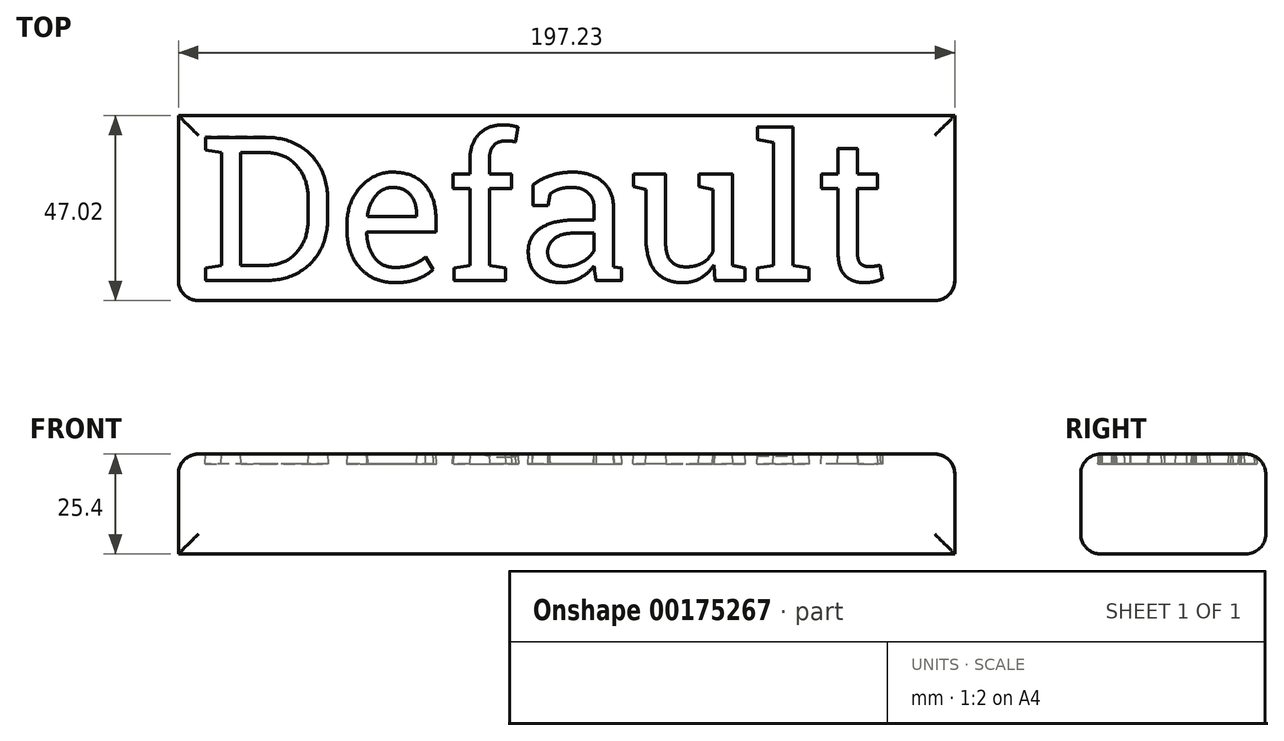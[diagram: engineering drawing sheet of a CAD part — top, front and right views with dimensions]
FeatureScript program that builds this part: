
annotation { "Feature Type Name" : "Feature", "Feature Type Description" : "" }
export const myFeature = defineFeature(function(context is Context, id is Id, definition is map)
    precondition{}
    {
        {
            var Q0;
            Q0=qCreatedBy(makeId("Top.planeOp"),FACE);
            var sketch = newSketch(context, id + "F0", { "sketchPlane" : qUnion([Q0])});
            skLineSegment(sketch, "E0.bottom", {"start": v(-91.51, 20.47) * mm, "end": v(105.72, 20.47) * mm});
            skLineSegment(sketch, "E0.top", {"start": v(-91.51, -26.55) * mm, "end": v(105.72, -26.55) * mm});
            skLineSegment(sketch, "E0.left", {"start": v(-91.51, 20.47) * mm, "end": v(-91.51, -26.55) * mm});
            skLineSegment(sketch, "E0.right", {"start": v(105.72, 20.47) * mm, "end": v(105.72, -26.55) * mm});
            skSolve(sketch);
        }
        {
            var Q0;
            Q0 = qSketchRegion(id + "F0", true);
            extrude(context, id + "F1", {"entities" : qUnion([Q0]), "depth" : 25.4 * mm});
        }
        {
            var Q0;
            Q0=makeQuery(id+"F1.opExtrude","CAP_FACE",FACE,{"disambiguationData":[OSD([sQuery(id+"F0.wireOp",EDGE,"E0.bottom"),sQuery(id+"F0.wireOp",EDGE,"E0.top"),sQuery(id+"F0.wireOp",EDGE,"E0.left"),sQuery(id+"F0.wireOp",EDGE,"E0.right")])],"isStart":false});
            var Q1;
            Q1=makeQuery(id+"F1.opExtrude","SWEPT_FACE",FACE,{"disambiguationData":[OSD([sQuery(id+"F0.wireOp",EDGE,"E0.top")])]});
            var Q2;
            Q2=makeQuery(id+"F1.opExtrude","CAP_EDGE",EDGE,{"disambiguationData":[OSD([sQuery(id+"F0.wireOp",EDGE,"E0.bottom")])],"isStart":true});
            fillet(context, id + "F2", {"entities" : qUnion([Q0, Q1, Q2]), "radius" : 5.08 * mm, "tangentPropagation" : true, "allowEdgeOverflow" : false});
        }
        {
            var Q0;
            Q0=makeQuery(id+"F1.opExtrude","CAP_FACE",FACE,{"disambiguationData":[OSD([sQuery(id+"F0.wireOp",EDGE,"E0.bottom"),sQuery(id+"F0.wireOp",EDGE,"E0.top"),sQuery(id+"F0.wireOp",EDGE,"E0.left"),sQuery(id+"F0.wireOp",EDGE,"E0.right")])],"isStart":false});
            var sketch = newSketch(context, id + "F3", { "sketchPlane" : qUnion([Q0])});
            skText(sketch, "E1", { "text": "Default", "fontName": "RobotoSlab-Regular.ttf"});
            const initialGuessF3  = {"E1": [-0.08643, -0.02147, 1, 0, 0.03686]};
            skSetInitialGuess(sketch, initialGuessF3);
            skSolve(sketch);
        }
        {
            var Q0;
            Q0 = qSketchRegion(id + "F3", true);
            extrude(context, id + "F4", {"entities" : qUnion([Q0]), "operationType" : NewBodyOperationType.REMOVE, "oppositeDirection" : true, "depth" : 2.54 * mm, "hasDraft" : true, "draftAngle" : 3 * degree});
        }
    });
